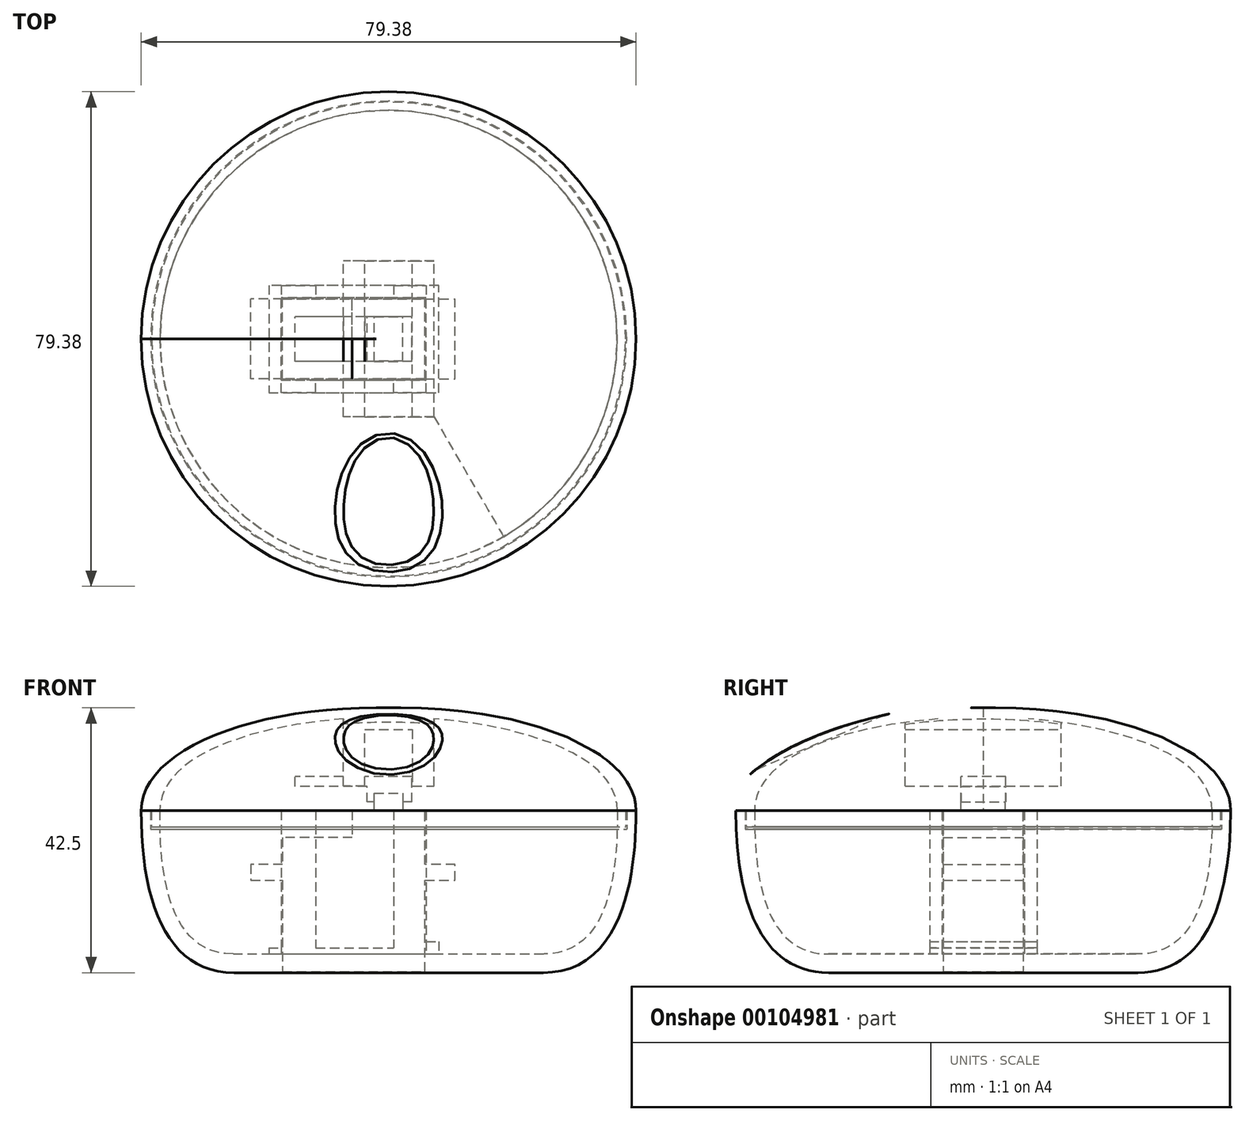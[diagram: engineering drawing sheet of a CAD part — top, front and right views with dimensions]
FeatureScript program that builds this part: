
annotation { "Feature Type Name" : "Feature", "Feature Type Description" : "" }
export const myFeature = defineFeature(function(context is Context, id is Id, definition is map)
    precondition{}
    {
        {
            var Q0;
            Q0=qCreatedBy(makeId("Front.planeOp"),FACE);
            var sketch = newSketch(context, id + "F0", { "sketchPlane" : qUnion([Q0])});
            skLineSegment(sketch, "E0", {"start": v(-62.74, 0) * mm, "end": v(62.74, 0) * mm, "construction": true});
            skLineSegment(sketch, "E1", {"start": v(0, -23) * mm, "end": v(24.93, -23) * mm});
            skFitSpline(sketch, "E2", {"points": [v(24.93, -23) * mm, v(36.69, 0) * mm], "startDerivative": vector(34.28, 0) * mm, "endDerivative": vector(0, 21.8) * mm});
            skLineSegment(sketch, "E3", {"start": v(0, -26) * mm, "end": v(24.8, -26) * mm});
            skFitSpline(sketch, "E4", {"points": [v(24.8, -26) * mm, v(39.69, 0) * mm], "startDerivative": vector(31.25, 0) * mm, "endDerivative": vector(0, 46.22) * mm});
            skLineSegment(sketch, "E5", {"start": v(0, -23) * mm, "end": v(0, -26) * mm});
            skLineSegment(sketch, "E6", {"start": v(36.69, 0) * mm, "end": v(39.69, 0) * mm});
            skLineSegment(sketch, "E7", {"start": v(38.19, 0) * mm, "end": v(38.19, -3) * mm});
            skLineSegment(sketch, "E8", {"start": v(38.19, -3) * mm, "end": v(36.65, -3) * mm});
            skLineSegment(sketch, "E9", {"start": v(39.69, 0) * mm, "end": v(39.69, 20.6) * mm, "construction": true});
            skSolve(sketch);
        }
        {
            var Q0;
            Q0=qCreatedBy(makeId("Front.planeOp"),FACE);
            var sketch = newSketch(context, id + "F1", { "sketchPlane" : qUnion([Q0])});
            skLineSegment(sketch, "E10", {"start": v(-17.02, -25.82) * mm, "end": v(5.84, -25.82) * mm});
            skLineSegment(sketch, "E11", {"start": v(5.84, -25.82) * mm, "end": v(5.84, -11.18) * mm});
            skLineSegment(sketch, "E12", {"start": v(5.84, -11.18) * mm, "end": v(10.67, -11.18) * mm});
            skLineSegment(sketch, "E13", {"start": v(10.67, -11.18) * mm, "end": v(10.67, -8.64) * mm});
            skLineSegment(sketch, "E14", {"start": v(10.67, -8.64) * mm, "end": v(5.84, -8.64) * mm});
            skLineSegment(sketch, "E15", {"start": v(5.84, -8.64) * mm, "end": v(5.84, 0) * mm});
            skLineSegment(sketch, "E16", {"start": v(5.84, 0) * mm, "end": v(-5.84, 0) * mm});
            skLineSegment(sketch, "E17", {"start": v(-5.84, 0) * mm, "end": v(-5.84, -4.32) * mm});
            skLineSegment(sketch, "E18", {"start": v(-5.84, -4.32) * mm, "end": v(-17.02, -4.32) * mm});
            skLineSegment(sketch, "E19", {"start": v(-17.02, -4.32) * mm, "end": v(-17.02, -8.64) * mm});
            skLineSegment(sketch, "E20", {"start": v(-17.02, -8.64) * mm, "end": v(-22.1, -8.64) * mm});
            skLineSegment(sketch, "E21", {"start": v(-22.1, -8.64) * mm, "end": v(-22.1, -11.18) * mm});
            skLineSegment(sketch, "E22", {"start": v(-22.1, -11.18) * mm, "end": v(-17.02, -11.18) * mm});
            skLineSegment(sketch, "E23", {"start": v(-17.02, -11.18) * mm, "end": v(-17.02, -25.82) * mm});
            skPoint(sketch, "E24", {"position": v(0, 0) * mm});
            skLineSegment(sketch, "E25", {"start": v(-2.29, 0) * mm, "end": v(-2.29, 2.8) * mm});
            skLineSegment(sketch, "E26", {"start": v(-2.29, 2.8) * mm, "end": v(2.29, 2.8) * mm});
            skLineSegment(sketch, "E27", {"start": v(2.29, 2.8) * mm, "end": v(2.29, 0) * mm});
            skLineSegment(sketch, "E28", {"start": v(0, 0) * mm, "end": v(0, 24.97) * mm, "construction": true});
            skPoint(sketch, "E29.firstSnap0", {"position": v(2.29, 1.4) * mm});
            skLineSegment(sketch, "E29.bottom", {"start": v(3.73, 1.4) * mm, "end": v(-3.47, 1.4) * mm});
            skLineSegment(sketch, "E29.top", {"start": v(3.73, 3.88) * mm, "end": v(-3.47, 3.88) * mm});
            skLineSegment(sketch, "E29.left", {"start": v(3.73, 1.4) * mm, "end": v(3.73, 3.88) * mm});
            skLineSegment(sketch, "E29.right", {"start": v(-3.47, 1.4) * mm, "end": v(-3.47, 3.88) * mm});
            skLineSegment(sketch, "E30.bottom", {"start": v(3.73, 3.88) * mm, "end": v(-14.97, 3.88) * mm});
            skLineSegment(sketch, "E30.top", {"start": v(3.73, 5.48) * mm, "end": v(-14.97, 5.48) * mm});
            skLineSegment(sketch, "E30.left", {"start": v(3.73, 3.88) * mm, "end": v(3.73, 5.48) * mm});
            skLineSegment(sketch, "E30.right", {"start": v(-14.97, 3.88) * mm, "end": v(-14.97, 5.48) * mm});
            skSolve(sketch);
        }
        {
            var Q0;
            Q0=makeQuery(id+"F1.imprint","IMPRINT",FACE,{"disambiguationData":[TD([[makeQuery(id+"F1.imprint","IMPRINT",EDGE,{"derivedFrom":sQuery(id+"F1.wireOp",EDGE,"E10")}),1.0]])]});
            extrude(context, id + "F2", {"entities" : qUnion([Q0]), "endBound" : BoundingType.SYMMETRIC, "depth" : 12.83 * mm});
        }
        {
            var Q0;
            {var subQ0=sQuery(id+"F1.wireOp",EDGE,"E25");Q0=makeQuery(id+"F1.imprint","IMPRINT",FACE,{"disambiguationData":[TD([[makeQuery(id+"F1.imprint","IMPRINT",EDGE,{"derivedFrom":subQ0}),-1.0]])]});}
            extrude(context, id + "F3", {"entities" : qUnion([Q0]), "operationType" : NewBodyOperationType.ADD, "endBound" : BoundingType.SYMMETRIC, "depth" : 7.11 * mm});
        }
        {
            var Q0;
            Q0=makeQuery(id+"F0.imprint","IMPRINT",FACE,{"disambiguationData":[TD([[makeQuery(id+"F0.imprint","IMPRINT",EDGE,{"derivedFrom":sQuery(id+"F0.wireOp",EDGE,"E1")}),-1.0]])]});
            var Q1;
            Q1=sQuery(id+"F1.wireOp",EDGE,"E28");
            revolve(context, id + "F4", {"entities" : qUnion([Q0]), "axis" : qUnion([Q1]), "revolveType" : RevolveType.FULL});
        }
        {
            var Q0;
            Q0=makeQuery(id+"F4.opRevolve","SWEPT_FACE",FACE,{"disambiguationData":[OSD([sQuery(id+"F0.wireOp",EDGE,"E1")])]});
            var sketch = newSketch(context, id + "F5", { "sketchPlane" : qUnion([Q0])});
            skLineSegment(sketch, "E31", {"start": v(-17.22, -6.61) * mm, "end": v(6.04, -6.61) * mm});
            skLineSegment(sketch, "E32", {"start": v(6.04, -6.61) * mm, "end": v(6.04, 6.61) * mm});
            skLineSegment(sketch, "E33", {"start": v(6.04, 6.61) * mm, "end": v(-17.22, 6.61) * mm});
            skLineSegment(sketch, "E34", {"start": v(-17.22, 6.61) * mm, "end": v(-17.22, -6.61) * mm});
            skLineSegment(sketch, "E35", {"start": v(8.04, 8.61) * mm, "end": v(-19.22, 8.61) * mm});
            skLineSegment(sketch, "E36", {"start": v(-19.22, 8.61) * mm, "end": v(-19.22, -8.61) * mm});
            skLineSegment(sketch, "E37", {"start": v(-19.22, -8.61) * mm, "end": v(8.04, -8.61) * mm});
            skLineSegment(sketch, "E38", {"start": v(8.04, -8.61) * mm, "end": v(8.04, 8.61) * mm});
            skLineSegment(sketch, "E39", {"start": v(-17.22, -6.61) * mm, "end": v(-17.22, -8.61) * mm});
            skLineSegment(sketch, "E40", {"start": v(-11.68, -6.61) * mm, "end": v(-11.68, -8.61) * mm});
            skLineSegment(sketch, "E41", {"start": v(6.04, -6.61) * mm, "end": v(6.04, -8.61) * mm});
            skLineSegment(sketch, "E42", {"start": v(0.8, -6.61) * mm, "end": v(0.8, -8.61) * mm});
            skLineSegment(sketch, "E43", {"start": v(6.04, -6.61) * mm, "end": v(8.04, -6.61) * mm});
            skLineSegment(sketch, "E44", {"start": v(6.04, 6.61) * mm, "end": v(8.04, 6.61) * mm});
            skLineSegment(sketch, "E45", {"start": v(-17.22, 6.61) * mm, "end": v(-17.22, 8.61) * mm});
            skLineSegment(sketch, "E46", {"start": v(-11.68, 6.61) * mm, "end": v(-11.68, 8.61) * mm});
            skPoint(sketch, "E46.startSnap0", {"position": v(-11.68, -7.61) * mm});
            skLineSegment(sketch, "E47", {"start": v(0.8, 6.61) * mm, "end": v(0.8, 8.61) * mm});
            skLineSegment(sketch, "E48", {"start": v(6.04, 6.61) * mm, "end": v(6.04, 8.61) * mm});
            skSolve(sketch);
        }
        {
            var Q0;
            {var subQ0=sQuery(id+"F5.wireOp",EDGE,"E39");Q0=makeQuery(id+"F5.imprint","IMPRINT",FACE,{"disambiguationData":[TD([[makeQuery(id+"F5.imprint","IMPRINT",EDGE,{"derivedFrom":subQ0}),1.0]])]});}
            var Q1;
            {var subQ0=sQuery(id+"F5.wireOp",EDGE,"E40");Q1=makeQuery(id+"F5.imprint","IMPRINT",FACE,{"disambiguationData":[TD([[makeQuery(id+"F5.imprint","IMPRINT",EDGE,{"derivedFrom":subQ0}),-1.0]])]});}
            var Q2;
            {var subQ0=sQuery(id+"F5.wireOp",EDGE,"E41");Q2=makeQuery(id+"F5.imprint","IMPRINT",FACE,{"disambiguationData":[TD([[makeQuery(id+"F5.imprint","IMPRINT",EDGE,{"derivedFrom":subQ0}),-1.0]])]});}
            var Q3;
            {var subQ2=sQuery(id+"F5.wireOp",EDGE,"E47");Q3=makeQuery(id+"F5.imprint","IMPRINT",FACE,{"disambiguationData":[TD([[makeQuery(id+"F5.imprint","IMPRINT",EDGE,{"derivedFrom":subQ2}),-1.0]])]});}
            var Q4;
            {var subQ0=sQuery(id+"F5.wireOp",EDGE,"E46");Q4=makeQuery(id+"F5.imprint","IMPRINT",FACE,{"disambiguationData":[TD([[makeQuery(id+"F5.imprint","IMPRINT",EDGE,{"derivedFrom":subQ0}),1.0]])]});}
            var Q5;
            {var subQ0=sQuery(id+"F5.wireOp",EDGE,"E45");Q5=makeQuery(id+"F5.imprint","IMPRINT",FACE,{"disambiguationData":[TD([[makeQuery(id+"F5.imprint","IMPRINT",EDGE,{"derivedFrom":subQ0}),-1.0]])]});}
            var Q6;
            Q6=makeQuery(id+"F4.opRevolve","SWEPT_FACE",FACE,{"disambiguationData":[OSD([sQuery(id+"F0.wireOp",EDGE,"E6")])]});
            extrude(context, id + "F6", {"entities" : qUnion([Q0, Q1, Q2, Q3, Q4, Q5]), "operationType" : NewBodyOperationType.ADD, "endBound" : BoundingType.UP_TO_SURFACE, "endBoundEntityFace" : qUnion([Q6]), "depth" : 2.54 * mm});
        }
        {
            var Q0;
            Q0=qCreatedBy(makeId("Front.planeOp"),FACE);
            var sketch = newSketch(context, id + "F7", { "sketchPlane" : qUnion([Q0])});
            skLineSegment(sketch, "E49", {"start": v(0, 16.5) * mm, "end": v(1.98, 16.5) * mm});
            skLineSegment(sketch, "E50", {"start": v(0, 15) * mm, "end": v(0, 15) * mm});
            skLineSegment(sketch, "E51", {"start": v(0, 15) * mm, "end": v(0, 16.5) * mm});
            skFitSpline(sketch, "E52", {"points": [v(0, 15) * mm, v(36.69, 0) * mm], "startDerivative": vector(54.37, 0) * mm, "endDerivative": vector(0, -29.65) * mm});
            skFitSpline(sketch, "E53", {"points": [v(1.98, 16.5) * mm, v(39.69, 0) * mm], "startDerivative": vector(62.96, 0) * mm, "endDerivative": vector(0, -28.06) * mm});
            skLineSegment(sketch, "E54", {"start": v(24.8, 30.13) * mm, "end": v(24.8, -30.66) * mm, "construction": true});
            skLineSegment(sketch, "E55", {"start": v(36.69, 0) * mm, "end": v(39.69, 0) * mm});
            skLineSegment(sketch, "E56", {"start": v(38.02, 0) * mm, "end": v(38.02, -2.6) * mm});
            skLineSegment(sketch, "E57", {"start": v(38.02, -2.6) * mm, "end": v(36.69, -2.6) * mm});
            skLineSegment(sketch, "E58", {"start": v(36.69, -2.6) * mm, "end": v(36.69, 0) * mm});
            skSolve(sketch);
        }
        {
            var Q0;
            Q0=qSketchRegion(id+"F7",true);
            var Q1;
            Q1=sQuery(id+"F1.wireOp",EDGE,"E28");
            revolve(context, id + "F8", {"entities" : qUnion([Q0]), "axis" : qUnion([Q1]), "revolveType" : RevolveType.FULL});
        }
        {
            var Q0;
            Q0=qCreatedBy(makeId("Front.planeOp"),FACE);
            var sketch = newSketch(context, id + "F9", { "sketchPlane" : qUnion([Q0])});
            skLineSegment(sketch, "E59", {"start": v(-3.8, 3.97) * mm, "end": v(-3.8, 13) * mm});
            skLineSegment(sketch, "E60", {"start": v(-3.8, 13) * mm, "end": v(3.81, 13) * mm});
            skLineSegment(sketch, "E61", {"start": v(3.81, 13) * mm, "end": v(3.81, 3.97) * mm});
            skLineSegment(sketch, "E62", {"start": v(3.81, 3.97) * mm, "end": v(7.27, 3.97) * mm});
            skLineSegment(sketch, "E63", {"start": v(7.27, 3.97) * mm, "end": v(7.27, 15.2) * mm});
            skLineSegment(sketch, "E64", {"start": v(-3.8, 3.97) * mm, "end": v(-7.27, 3.97) * mm});
            skLineSegment(sketch, "E65", {"start": v(-7.27, 3.97) * mm, "end": v(-7.27, 15.2) * mm});
            skLineSegment(sketch, "E66", {"start": v(-7.27, 15.2) * mm, "end": v(7.27, 15.2) * mm});
            skSolve(sketch);
        }
        {
            var Q0;
            Q0=makeQuery(id+"F9.imprint","IMPRINT",FACE,{"disambiguationData":[TD([[makeQuery(id+"F9.imprint","IMPRINT",EDGE,{"derivedFrom":sQuery(id+"F9.wireOp",EDGE,"E59")}),1.0]])]});
            extrude(context, id + "F10", {"entities" : qUnion([Q0]), "operationType" : NewBodyOperationType.ADD, "endBound" : BoundingType.SYMMETRIC, "depth" : 25 * mm});
        }
        {
            var Q0;
            Q0=makeQuery(id+"F5.imprint","IMPRINT",FACE,{"disambiguationData":[TD([[makeQuery(id+"F5.imprint","IMPRINT",EDGE,{"derivedFrom":sQuery(id+"F5.wireOp",EDGE,"E32")}),-1.0]])]});
            var Q1;
            {var subQ3=sQuery(id+"F5.wireOp",EDGE,"E41");Q1=makeQuery(id+"F5.imprint","IMPRINT",FACE,{"disambiguationData":[TD([[makeQuery(id+"F5.imprint","IMPRINT",EDGE,{"derivedFrom":subQ3}),1.0]])]});}
            var Q2;
            {var subQ4=sQuery(id+"F5.wireOp",EDGE,"E44");Q2=makeQuery(id+"F5.imprint","IMPRINT",FACE,{"disambiguationData":[TD([[makeQuery(id+"F5.imprint","IMPRINT",EDGE,{"derivedFrom":subQ4}),1.0]])]});}
            extrude(context, id + "F11", {"entities" : qUnion([Q0, Q1, Q2]), "operationType" : NewBodyOperationType.ADD, "depth" : 2 * mm});
        }
        {
            var Q0;
            {var subQ0=sQuery(id+"F5.wireOp",EDGE,"E40");Q0=makeQuery(id+"F5.imprint","IMPRINT",FACE,{"disambiguationData":[TD([[makeQuery(id+"F5.imprint","IMPRINT",EDGE,{"derivedFrom":subQ0}),1.0]])]});}
            var Q1;
            {var subQ0=sQuery(id+"F5.wireOp",EDGE,"E46");Q1=makeQuery(id+"F5.imprint","IMPRINT",FACE,{"disambiguationData":[TD([[makeQuery(id+"F5.imprint","IMPRINT",EDGE,{"derivedFrom":subQ0}),-1.0]])]});}
            var Q2;
            Q2=makeQuery(id+"F5.imprint","IMPRINT",FACE,{"disambiguationData":[TD([[makeQuery(id+"F5.imprint","IMPRINT",EDGE,{"derivedFrom":sQuery(id+"F5.wireOp",EDGE,"E34")}),-1.0]])]});
            extrude(context, id + "F12", {"entities" : qUnion([Q0, Q1, Q2]), "operationType" : NewBodyOperationType.ADD, "depth" : 1 * mm});
        }
        {
            var Q0;
            {var subQ4=sQuery(id+"F1.wireOp",EDGE,"E26");Q0=makeQuery(id+"F1.imprint","IMPRINT",FACE,{"disambiguationData":[TD([[makeQuery(id+"F1.imprint","IMPRINT",EDGE,{"derivedFrom":subQ4}),1.0]])]});}
            var Q1;
            Q1=makeQuery(id+"F1.imprint","IMPRINT",FACE,{"disambiguationData":[TD([[makeQuery(id+"F1.imprint","IMPRINT",EDGE,{"derivedFrom":sQuery(id+"F1.wireOp",EDGE,"E30.top")}),1.0]])]});
            extrude(context, id + "F13", {"entities" : qUnion([Q0, Q1]), "operationType" : NewBodyOperationType.ADD, "endBound" : BoundingType.SYMMETRIC, "depth" : 7.2 * mm});
        }
        {
            var Q0;
            Q0=qCreatedBy(makeId("Right.planeOp"),FACE);
            var sketch = newSketch(context, id + "F14", { "sketchPlane" : qUnion([Q0])});
            skLineSegment(sketch, "E67", {"start": v(-8.53, 22.2) * mm, "end": v(-50.62, 4.34) * mm});
            skSolve(sketch);
        }
        {
            var Q0;
            Q0=sQuery(id+"F14.wireOp",EDGE,"E67");
            var Q1;
            Q1=sQuery(id+"F14.wireOp",VERTEX,"E67.end");
            cPlane(context, id + "F15", {"entities" : qUnion([Q0, Q1]), "cplaneType" : CPlaneType.LINE_POINT, "offset" : 25 * mm, "width" : 150 * mm, "height" : 150 * mm});
        }
        {
            var Q0;
            Q0=qCreatedBy(id+"F15.planeOp",FACE);
            var sketch = newSketch(context, id + "F16", { "sketchPlane" : qUnion([Q0])});
            skEllipse(sketch, "E68", {"center": v(0, 23.77) * mm, "majorRadius": 10 * mm, "minorRadius": 3.5 * mm, "majorAxis": v(1, 0)});
            skSolve(sketch);
        }
        {
            var Q0;
            Q0=makeQuery(id+"F16.imprint","IMPRINT",FACE,{"disambiguationData":[TD([[makeQuery(id+"F16.imprint","IMPRINT",EDGE,{"derivedFrom":sQuery(id+"F16.wireOp",EDGE,"E68")}),1.0]])]});
            extrude(context, id + "F17", {"entities" : qUnion([Q0]), "operationType" : NewBodyOperationType.REMOVE, "oppositeDirection" : true, "depth" : 50 * mm});
        }
        {
            var Q0;
            Q0=makeQuery(id+"F17.boolean.opBoolean","INTERSECT",EDGE,{"derivedFrom":[makeQuery(id+"F8.opRevolve","SWEPT_FACE",FACE,{"disambiguationData":[OSD([sQuery(id+"F7.wireOp",EDGE,"E53")])]}),makeQuery(id+"F17.opExtrude","SWEPT_FACE",FACE,{"disambiguationData":[OSD([sQuery(id+"F16.wireOp",EDGE,"E68")])]})]});
            fillet(context, id + "F18", {"entities" : qUnion([Q0]), "radius" : 3 * mm, "tangentPropagation" : true, "allowEdgeOverflow" : false});
        }
    });
